# Revit family: Legrand Marina square version references 036951 to 036972
name_source: partatom
category: Installations électriques
revit_build: Autodesk Revit 2018 (Build: 20170223_1515(x64)
units: mm (PartAtom-declared; Revit-internal decimal feet)

## family parameters
Basée sur le plan de construction = Non
Conserver l'orientation des annotations = Non
Cote de connecteur circulaire = Utiliser le diamètre
Couper avec des vides une fois chargée = Non
Numéro OmniClass = 23.80.00.00
Partagée = Non
Point de calcul de pièce = Non
Titre OmniClass = Electric Power and Lighting
Toujours verticalement = Oui
Type d'élément = Normal

## types (8) — shared parameters
ETIM Class 6.0 = EC000058
Fabricant = Legrand
General Conditions of Use = https://export.legrand.com
Glass door = Non
Horizontal version = Non
IK = 10
IP = 66
Material = Metallic
Number of door = 1
RAL = 7035
Square version = Oui
URL = www.legrand.fr
Vertical version = Non

## per-type parameters (varying)
| type | Cabinet 036951 | Cabinet 036955 | Cabinet 036957 | Cabinet 036959 | Cabinet 036962 | Cabinet 036964 | Cabinet 036968 | Cabinet 036972 | Length | depth | height | weight |
| Legrand Atlantic 036959 | Non | Non | Non | Oui | Non | Non | Non | Non | 500 mm  [stored 1.64042 ft] | 200 mm  [stored 0.656168 ft] | 500 mm  [stored 1.64042 ft] | 19.80 kg |
| Legrand Atlantic 036951 | Oui | Non | Non | Non | Non | Non | Non | Non | 300 mm | 160 mm  [stored 0.524934 ft] | 300 mm | 4.90 kg |
| Legrand Atlantic 036955 | Non | Oui | Non | Non | Non | Non | Non | Non | 300 mm | 200 mm  [stored 0.656168 ft] | 300 mm | 5.60 kg |
| Legrand Atlantic 036957 | Non | Non | Oui | Non | Non | Non | Non | Non | 400 mm  [stored 1.31234 ft] | 200 mm  [stored 0.656168 ft] | 400 mm  [stored 1.31234 ft] | 8.30 kg |
| Legrand Atlantic 036962 | Non | Non | Non | Non | Oui | Non | Non | Non | 500 mm  [stored 1.64042 ft] | 250 mm  [stored 0.82021 ft] | 500 mm  [stored 1.64042 ft] | 17.80 kg |
| Legrand Atlantic 036964 | Non | Non | Non | Non | Non | Oui | Non | Non | 600 mm | 250 mm  [stored 0.82021 ft] | 600 mm | 25.30 kg |
| Legrand Atlantic 036968 | Non | Non | Non | Non | Non | Non | Oui | Non | 800 mm  [stored 2.62467 ft] | 300 mm | 800 mm  [stored 2.62467 ft] | 47.10 kg |
| Legrand Atlantic 036972 | Non | Non | Non | Non | Non | Non | Non | Oui | 600 mm | 400 mm  [stored 1.31234 ft] | 600 mm | 29.60 kg |

note: column(s) folded — value = type name in every type: Description

note: [stored X ft] marks values corroborated as IEEE doubles in the binary element streams (Revit-internal decimal feet)
